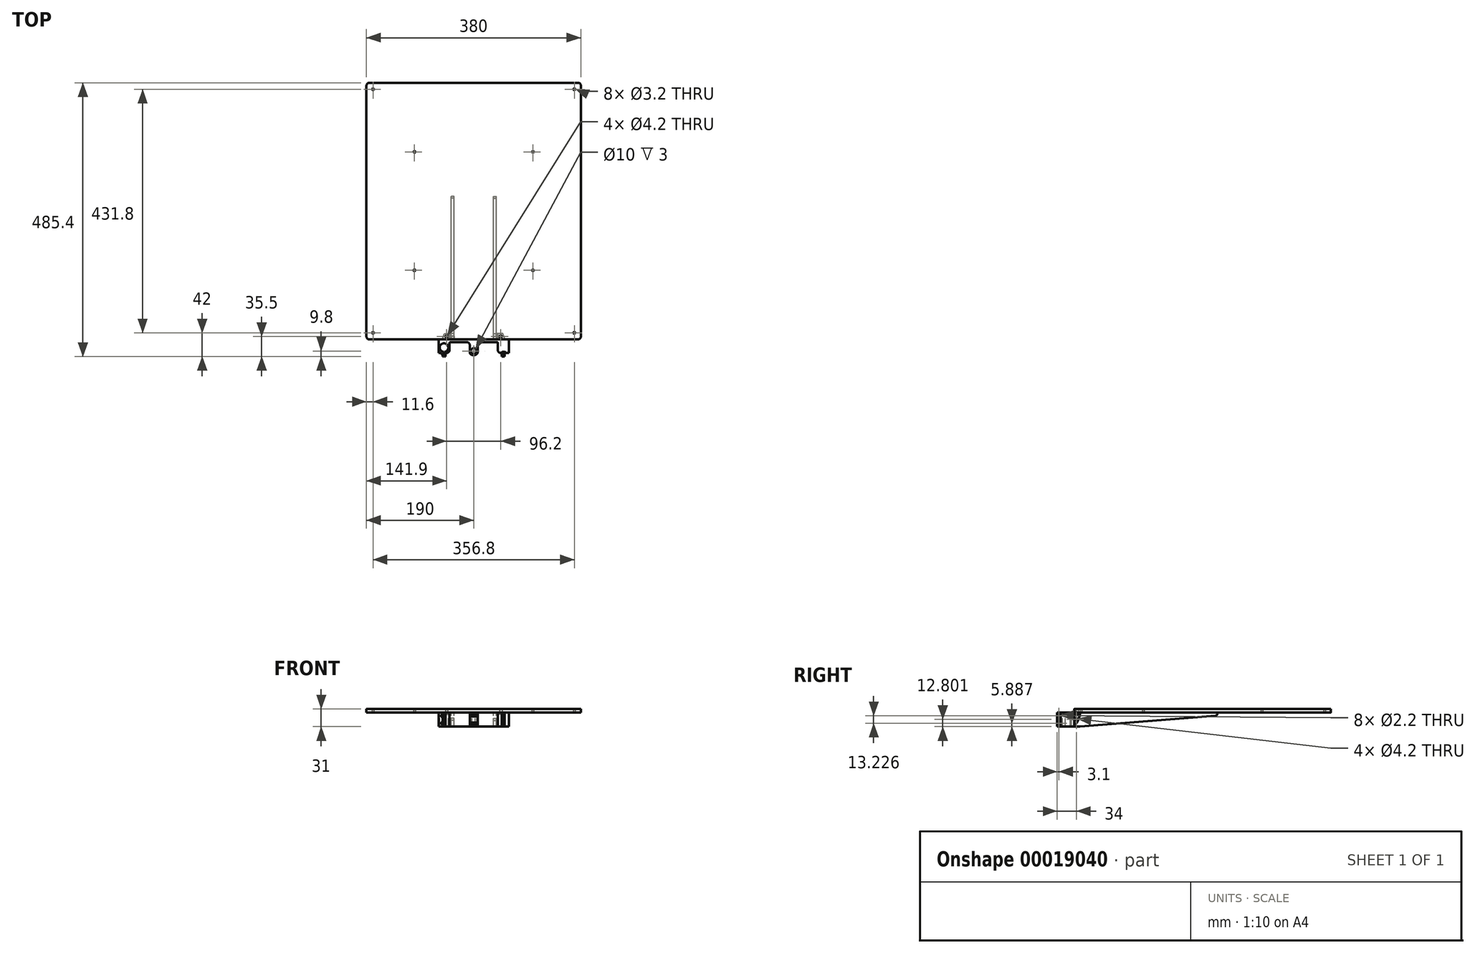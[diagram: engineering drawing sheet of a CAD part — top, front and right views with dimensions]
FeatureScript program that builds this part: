
annotation { "Feature Type Name" : "Feature", "Feature Type Description" : "" }
export const myFeature = defineFeature(function(context is Context, id is Id, definition is map)
    precondition{}
    {
        {
            var Q0;
            Q0=qCreatedBy(makeId("Top.planeOp"),FACE);
            var sketch = newSketch(context, id + "F0", { "sketchPlane" : qUnion([Q0])});
            skLineSegment(sketch, "E0.bottom", {"start": v(62.2, 0) * mm, "end": v(-62.2, 0) * mm});
            skLineSegment(sketch, "E0.top", {"start": v(62.2, 5) * mm, "end": v(-62.2, 5) * mm});
            skLineSegment(sketch, "E0.left", {"start": v(62.2, 0) * mm, "end": v(62.2, 5) * mm});
            skLineSegment(sketch, "E0.right", {"start": v(-62.2, 0) * mm, "end": v(-62.2, 5) * mm});
            skLineSegment(sketch, "E1", {"start": v(-55.38, 5) * mm, "end": v(-51.67, 15.2) * mm});
            skLineSegment(sketch, "E2", {"start": v(-51.67, 15.2) * mm, "end": v(-43, 15.2) * mm});
            skLineSegment(sketch, "E3", {"start": v(-43, 15.2) * mm, "end": v(-43, 5) * mm});
            skLineSegment(sketch, "E4", {"start": v(-48.1, 15.2) * mm, "end": v(-48.1, 5) * mm, "construction": true});
            skCircle(sketch, "E5", {"center": v(-48.1, 10.1) * mm, "radius": 2.1 * mm});
            skCircle(sketch, "E6", {"center": v(-52.6, -9.6) * mm, "radius": 7.6 * mm});
            skLineSegment(sketch, "E7", {"start": v(0, 10.4) * mm, "end": v(0, -22.6) * mm, "construction": true});
            skLineSegment(sketch, "E8.MirrorCS", {"start": v(55.38, 5) * mm, "end": v(51.67, 15.2) * mm});
            skLineSegment(sketch, "E9.MirrorCS", {"start": v(43, 15.2) * mm, "end": v(43, 5) * mm});
            skLineSegment(sketch, "E10.MirrorCS", {"start": v(51.67, 15.2) * mm, "end": v(43, 15.2) * mm});
            skCircle(sketch, "E11.MirrorC", {"center": v(48.1, 10.1) * mm, "radius": 2.1 * mm});
            skCircle(sketch, "E12.MirrorC", {"center": v(52.6, -9.6) * mm, "radius": 7.6 * mm});
            skCircle(sketch, "E13", {"center": v(0, -15.6) * mm, "radius": 5 * mm});
            skLineSegment(sketch, "E14", {"start": v(-62.2, 0) * mm, "end": v(-62.2, -19.2) * mm});
            skLineSegment(sketch, "E15", {"start": v(-62.2, -19.2) * mm, "end": v(-43, -19.2) * mm});
            skLineSegment(sketch, "E16", {"start": v(-43, -19.2) * mm, "end": v(-43, 5) * mm});
            skLineSegment(sketch, "E17.MirrorCS", {"start": v(62.2, -19.2) * mm, "end": v(43, -19.2) * mm});
            skLineSegment(sketch, "E18.MirrorCS", {"start": v(43, -19.2) * mm, "end": v(43, 5) * mm});
            skLineSegment(sketch, "E19.MirrorCS", {"start": v(62.2, 0) * mm, "end": v(62.2, -19.2) * mm});
            skCircle(sketch, "E20.cCircle", {"center": v(0, -15.6) * mm, "radius": 5 * mm, "construction": true});
            skLineSegment(sketch, "E20.0", {"start": v(-2.89, -20.6) * mm, "end": v(-5.77, -15.6) * mm});
            skLineSegment(sketch, "E20.1", {"start": v(-5.77, -15.6) * mm, "end": v(-2.89, -10.6) * mm});
            skLineSegment(sketch, "E20.2", {"start": v(-2.89, -10.6) * mm, "end": v(2.89, -10.6) * mm});
            skLineSegment(sketch, "E20.3", {"start": v(2.89, -10.6) * mm, "end": v(5.77, -15.6) * mm});
            skLineSegment(sketch, "E20.4", {"start": v(5.77, -15.6) * mm, "end": v(2.89, -20.6) * mm});
            skLineSegment(sketch, "E20.5", {"start": v(2.89, -20.6) * mm, "end": v(-2.89, -20.6) * mm});
            skPoint(sketch, "E20.0.midPoint", {"position": v(-4.33, -18.1) * mm});
            skLineSegment(sketch, "E21", {"start": v(-7, 0) * mm, "end": v(-7, -22.6) * mm});
            skLineSegment(sketch, "E22", {"start": v(-7, -22.6) * mm, "end": v(7, -22.6) * mm});
            skLineSegment(sketch, "E23", {"start": v(7, -22.6) * mm, "end": v(7, 0) * mm});
            skLineSegment(sketch, "E24", {"start": v(-52.6, -9.6) * mm, "end": v(52.6, -9.6) * mm, "construction": true});
            skLineSegment(sketch, "E25", {"start": v(-55.1, -16.78) * mm, "end": v(-55.1, -25.4) * mm});
            skLineSegment(sketch, "E26", {"start": v(-55.1, -25.4) * mm, "end": v(-53.1, -25.4) * mm});
            skLineSegment(sketch, "E27", {"start": v(-53.1, -25.4) * mm, "end": v(-53.1, -17.18) * mm});
            skLineSegment(sketch, "E28", {"start": v(-52.6, -34.95) * mm, "end": v(-52.6, -9.6) * mm, "construction": true});
            skLineSegment(sketch, "E29.MirrorCS", {"start": v(-50.1, -16.78) * mm, "end": v(-50.1, -25.4) * mm});
            skLineSegment(sketch, "E30.MirrorCS", {"start": v(-52.1, -25.4) * mm, "end": v(-52.1, -17.18) * mm});
            skLineSegment(sketch, "E31.MirrorCS", {"start": v(-50.1, -25.4) * mm, "end": v(-52.1, -25.4) * mm});
            skLineSegment(sketch, "E32.MirrorCS", {"start": v(55.1, -16.78) * mm, "end": v(55.1, -25.4) * mm});
            skLineSegment(sketch, "E33.MirrorCS", {"start": v(53.1, -25.4) * mm, "end": v(53.1, -17.18) * mm});
            skLineSegment(sketch, "E34.MirrorCS", {"start": v(52.1, -25.4) * mm, "end": v(52.1, -17.18) * mm});
            skLineSegment(sketch, "E35.MirrorCS", {"start": v(50.1, -16.78) * mm, "end": v(50.1, -25.4) * mm});
            skLineSegment(sketch, "E36.MirrorCS", {"start": v(50.1, -25.4) * mm, "end": v(52.1, -25.4) * mm});
            skLineSegment(sketch, "E37.MirrorCS", {"start": v(55.1, -25.4) * mm, "end": v(53.1, -25.4) * mm});
            skLineSegment(sketch, "E38", {"start": v(0, -10.6) * mm, "end": v(0, 0) * mm, "construction": true});
            skLineSegment(sketch, "E39.bottom", {"start": v(-185, 5) * mm, "end": v(185, 5) * mm});
            skLineSegment(sketch, "E39.top", {"start": v(-185, 460) * mm, "end": v(185, 460) * mm});
            skLineSegment(sketch, "E39.left", {"start": v(-190, 455) * mm, "end": v(-190, 10) * mm});
            skLineSegment(sketch, "E39.right", {"start": v(190, 455) * mm, "end": v(190, 10) * mm});
            skPoint(sketch, "E40.visualSharp", {"position": v(-190, 5) * mm});
            skArc(sketch, "E40.filletArc", {"start": v(-190, 10) * mm, "mid": v(-188.54, 6.46) * mm, "end": v(-185, 5) * mm});
            skPoint(sketch, "E41.visualSharp", {"position": v(190, 5) * mm});
            skArc(sketch, "E41.filletArc", {"start": v(185, 5) * mm, "mid": v(188.54, 6.46) * mm, "end": v(190, 10) * mm});
            skPoint(sketch, "E42.visualSharp", {"position": v(190, 460) * mm});
            skArc(sketch, "E42.filletArc", {"start": v(190, 455) * mm, "mid": v(188.54, 458.54) * mm, "end": v(185, 460) * mm});
            skPoint(sketch, "E43.visualSharp", {"position": v(-190, 460) * mm});
            skArc(sketch, "E43.filletArc", {"start": v(-185, 460) * mm, "mid": v(-188.54, 458.54) * mm, "end": v(-190, 455) * mm});
            skPoint(sketch, "E44.endSnap0", {"position": v(53.53, 10.1) * mm});
            skLineSegment(sketch, "E45", {"start": v(52.6, -2) * mm, "end": v(52.6, 10.4) * mm, "construction": true});
            skLineSegment(sketch, "E46", {"start": v(52.6, 10.4) * mm, "end": v(0, 10.4) * mm, "construction": true});
            skLineSegment(sketch, "E47", {"start": v(-190, 232.5) * mm, "end": v(190, 232.5) * mm, "construction": true});
            skLineSegment(sketch, "E48.rect.bottom", {"start": v(-105, 337.5) * mm, "end": v(105, 337.5) * mm, "construction": true});
            skLineSegment(sketch, "E48.rect.top", {"start": v(-105, 127.5) * mm, "end": v(105, 127.5) * mm, "construction": true});
            skLineSegment(sketch, "E48.rect.left", {"start": v(-105, 337.5) * mm, "end": v(-105, 127.5) * mm, "construction": true});
            skLineSegment(sketch, "E48.rect.right", {"start": v(105, 337.5) * mm, "end": v(105, 127.5) * mm, "construction": true});
            skPoint(sketch, "E48.rect.middle", {"position": v(0, 232.5) * mm});
            skCircle(sketch, "E49", {"center": v(-105, 337.5) * mm, "radius": 1.6 * mm});
            skCircle(sketch, "E50", {"center": v(105, 337.5) * mm, "radius": 1.6 * mm});
            skCircle(sketch, "E51", {"center": v(105, 127.5) * mm, "radius": 1.6 * mm});
            skCircle(sketch, "E52", {"center": v(-105, 127.5) * mm, "radius": 1.6 * mm});
            skCircle(sketch, "E53", {"center": v(-178.4, 448.4) * mm, "radius": 1.6 * mm});
            skCircle(sketch, "E54", {"center": v(178.4, 448.4) * mm, "radius": 1.6 * mm});
            skCircle(sketch, "E55", {"center": v(178.4, 16.6) * mm, "radius": 1.6 * mm});
            skCircle(sketch, "E56", {"center": v(-178.4, 16.6) * mm, "radius": 1.6 * mm});
            skSolve(sketch);
        }
        {
            var Q0;
            Q0=makeQuery(id+"F0.imprint","IMPRINT",FACE,{"disambiguationData":[TD([[makeQuery(id+"F0.imprint","IMPRINT",EDGE,{"derivedFrom":sQuery(id+"F0.wireOp",EDGE,"E0.bottom")}),-1.0]])]});
            var Q1;
            {var subQ5=sQuery(id+"F0.wireOp",EDGE,"E0.right");Q1=makeQuery(id+"F0.imprint","IMPRINT",FACE,{"disambiguationData":[TD([[makeQuery(id+"F0.imprint","IMPRINT",EDGE,{"derivedFrom":subQ5}),-1.0]])]});}
            var Q2;
            {var subQ5=sQuery(id+"F0.wireOp",EDGE,"E0.left");Q2=makeQuery(id+"F0.imprint","IMPRINT",FACE,{"disambiguationData":[TD([[makeQuery(id+"F0.imprint","IMPRINT",EDGE,{"derivedFrom":subQ5}),1.0]])]});}
            var Q3;
            {var subQ10=sQuery(id+"F0.wireOp",EDGE,"E14");Q3=makeQuery(id+"F0.imprint","IMPRINT",FACE,{"disambiguationData":[TD([[makeQuery(id+"F0.imprint","IMPRINT",EDGE,{"derivedFrom":subQ10}),1.0]])]});}
            var Q4;
            {var subQ3=sQuery(id+"F0.wireOp",EDGE,"E6");var subQ5=sQuery(id+"F0.wireOp",EDGE,"E29.MirrorCS");var subQ7=makeQuery(id+"F0.imprint","INTERSECT",VERTEX,{"derivedFrom":[subQ3,subQ5]});Q4=makeQuery(id+"F0.imprint","IMPRINT",FACE,{"disambiguationData":[TD([[makeQuery(id+"F0.imprint","IMPRINT",EDGE,{"disambiguationData":[TD([[subQ7,1.0]])],"derivedFrom":subQ3}),-1.0]])]});}
            var Q5;
            {var subQ3=sQuery(id+"F0.wireOp",EDGE,"E6");var subQ5=sQuery(id+"F0.wireOp",EDGE,"E25");var subQ7=makeQuery(id+"F0.imprint","INTERSECT",VERTEX,{"derivedFrom":[subQ3,subQ5]});Q5=makeQuery(id+"F0.imprint","IMPRINT",FACE,{"disambiguationData":[TD([[makeQuery(id+"F0.imprint","IMPRINT",EDGE,{"disambiguationData":[TD([[subQ7,-1.0]])],"derivedFrom":subQ3}),-1.0]])]});}
            var Q6;
            {var subQ3=sQuery(id+"F0.wireOp",EDGE,"E26");Q6=makeQuery(id+"F0.imprint","IMPRINT",FACE,{"disambiguationData":[TD([[makeQuery(id+"F0.imprint","IMPRINT",EDGE,{"derivedFrom":subQ3}),1.0]])]});}
            var Q7;
            {var subQ0=sQuery(id+"F0.wireOp",EDGE,"E31.MirrorCS");Q7=makeQuery(id+"F0.imprint","IMPRINT",FACE,{"disambiguationData":[TD([[makeQuery(id+"F0.imprint","IMPRINT",EDGE,{"derivedFrom":subQ0}),-1.0]])]});}
            var Q8;
            {var subQ12=sQuery(id+"F0.wireOp",EDGE,"E19.MirrorCS");Q8=makeQuery(id+"F0.imprint","IMPRINT",FACE,{"disambiguationData":[TD([[makeQuery(id+"F0.imprint","IMPRINT",EDGE,{"derivedFrom":subQ12}),-1.0]])]});}
            var Q9;
            {var subQ3=sQuery(id+"F0.wireOp",EDGE,"E12.MirrorC");var subQ5=sQuery(id+"F0.wireOp",EDGE,"E32.MirrorCS");var subQ7=makeQuery(id+"F0.imprint","INTERSECT",VERTEX,{"derivedFrom":[subQ3,subQ5]});Q9=makeQuery(id+"F0.imprint","IMPRINT",FACE,{"disambiguationData":[TD([[makeQuery(id+"F0.imprint","IMPRINT",EDGE,{"disambiguationData":[TD([[subQ7,-1.0]])],"derivedFrom":subQ3}),1.0]])]});}
            var Q10;
            {var subQ3=sQuery(id+"F0.wireOp",EDGE,"E12.MirrorC");var subQ5=sQuery(id+"F0.wireOp",EDGE,"E34.MirrorCS");var subQ7=makeQuery(id+"F0.imprint","INTERSECT",VERTEX,{"derivedFrom":[subQ3,subQ5]});Q10=makeQuery(id+"F0.imprint","IMPRINT",FACE,{"disambiguationData":[TD([[makeQuery(id+"F0.imprint","IMPRINT",EDGE,{"disambiguationData":[TD([[subQ7,-1.0]])],"derivedFrom":subQ3}),1.0]])]});}
            var Q11;
            {var subQ0=sQuery(id+"F0.wireOp",EDGE,"E36.MirrorCS");Q11=makeQuery(id+"F0.imprint","IMPRINT",FACE,{"disambiguationData":[TD([[makeQuery(id+"F0.imprint","IMPRINT",EDGE,{"derivedFrom":subQ0}),1.0]])]});}
            var Q12;
            {var subQ3=sQuery(id+"F0.wireOp",EDGE,"E37.MirrorCS");Q12=makeQuery(id+"F0.imprint","IMPRINT",FACE,{"disambiguationData":[TD([[makeQuery(id+"F0.imprint","IMPRINT",EDGE,{"derivedFrom":subQ3}),-1.0]])]});}
            var Q13;
            {var subQ10=sQuery(id+"F0.wireOp",EDGE,"E21");Q13=makeQuery(id+"F0.imprint","IMPRINT",FACE,{"disambiguationData":[TD([[makeQuery(id+"F0.imprint","IMPRINT",EDGE,{"derivedFrom":subQ10}),1.0]])]});}
            var Q14;
            {var subQ0=sQuery(id+"F0.wireOp",EDGE,"E20.2");var subQ1=sQuery(id+"F0.wireOp",EDGE,"E13");var subQ2=makeQuery(id+"F0.imprint","INTERSECT",VERTEX,{"derivedFrom":[subQ1,subQ0]});Q14=makeQuery(id+"F0.imprint","IMPRINT",FACE,{"disambiguationData":[TD([[makeQuery(id+"F0.imprint","IMPRINT",EDGE,{"disambiguationData":[TD([[subQ2,-1.0]])],"derivedFrom":subQ1}),-1.0]])]});}
            var Q15;
            {var subQ1=sQuery(id+"F0.wireOp",EDGE,"E13");var subQ3=sQuery(id+"F0.wireOp",EDGE,"E20.2");var subQ5=makeQuery(id+"F0.imprint","INTERSECT",VERTEX,{"derivedFrom":[subQ1,subQ3]});Q15=makeQuery(id+"F0.imprint","IMPRINT",FACE,{"disambiguationData":[TD([[makeQuery(id+"F0.imprint","IMPRINT",EDGE,{"disambiguationData":[TD([[subQ5,1.0]])],"derivedFrom":subQ1}),-1.0]])]});}
            var Q16;
            {var subQ0=sQuery(id+"F0.wireOp",EDGE,"E20.1");var subQ1=sQuery(id+"F0.wireOp",EDGE,"E13");var subQ2=makeQuery(id+"F0.imprint","INTERSECT",VERTEX,{"derivedFrom":[subQ1,subQ0]});Q16=makeQuery(id+"F0.imprint","IMPRINT",FACE,{"disambiguationData":[TD([[makeQuery(id+"F0.imprint","IMPRINT",EDGE,{"disambiguationData":[TD([[subQ2,-1.0]])],"derivedFrom":subQ1}),-1.0]])]});}
            var Q17;
            {var subQ1=sQuery(id+"F0.wireOp",EDGE,"E13");var subQ3=sQuery(id+"F0.wireOp",EDGE,"E20.3");var subQ5=makeQuery(id+"F0.imprint","INTERSECT",VERTEX,{"derivedFrom":[subQ1,subQ3]});Q17=makeQuery(id+"F0.imprint","IMPRINT",FACE,{"disambiguationData":[TD([[makeQuery(id+"F0.imprint","IMPRINT",EDGE,{"disambiguationData":[TD([[subQ5,1.0]])],"derivedFrom":subQ1}),-1.0]])]});}
            var Q18;
            {var subQ1=sQuery(id+"F0.wireOp",EDGE,"E13");var subQ3=sQuery(id+"F0.wireOp",EDGE,"E20.0");var subQ5=makeQuery(id+"F0.imprint","INTERSECT",VERTEX,{"derivedFrom":[subQ1,subQ3]});Q18=makeQuery(id+"F0.imprint","IMPRINT",FACE,{"disambiguationData":[TD([[makeQuery(id+"F0.imprint","IMPRINT",EDGE,{"disambiguationData":[TD([[subQ5,-1.0]])],"derivedFrom":subQ1}),-1.0]])]});}
            var Q19;
            {var subQ0=sQuery(id+"F0.wireOp",EDGE,"E20.5");var subQ1=sQuery(id+"F0.wireOp",EDGE,"E13");var subQ2=makeQuery(id+"F0.imprint","INTERSECT",VERTEX,{"derivedFrom":[subQ1,subQ0]});Q19=makeQuery(id+"F0.imprint","IMPRINT",FACE,{"disambiguationData":[TD([[makeQuery(id+"F0.imprint","IMPRINT",EDGE,{"disambiguationData":[TD([[subQ2,-1.0]])],"derivedFrom":subQ1}),-1.0]])]});}
            extrude(context, id + "F1", {"entities" : qUnion([Q0, Q1, Q2, Q3, Q4, Q5, Q6, Q7, Q8, Q9, Q10, Q11, Q12, Q13, Q14, Q15, Q16, Q17, Q18, Q19]), "oppositeDirection" : true, "depth" : 25 * mm});
        }
        {
            var Q0;
            {var subQ1=sQuery(id+"F0.wireOp",EDGE,"E1");Q0=makeQuery(id+"F0.imprint","IMPRINT",FACE,{"disambiguationData":[TD([[makeQuery(id+"F0.imprint","IMPRINT",EDGE,{"derivedFrom":subQ1}),-1.0]])]});}
            var Q1;
            {var subQ1=sQuery(id+"F0.wireOp",EDGE,"E8.MirrorCS");Q1=makeQuery(id+"F0.imprint","IMPRINT",FACE,{"disambiguationData":[TD([[makeQuery(id+"F0.imprint","IMPRINT",EDGE,{"derivedFrom":subQ1}),1.0]])]});}
            extrude(context, id + "F2", {"entities" : qUnion([Q0, Q1]), "operationType" : NewBodyOperationType.ADD, "oppositeDirection" : true, "depth" : 3 * mm});
        }
        {
            var Q0;
            {var subQ0=sQuery(id+"F0.wireOp",EDGE,"E20.2");var subQ1=sQuery(id+"F0.wireOp",EDGE,"E13");var subQ2=makeQuery(id+"F0.imprint","INTERSECT",VERTEX,{"derivedFrom":[subQ1,subQ0]});Q0=makeQuery(id+"F0.imprint","IMPRINT",FACE,{"disambiguationData":[TD([[makeQuery(id+"F0.imprint","IMPRINT",EDGE,{"disambiguationData":[TD([[subQ2,-1.0]])],"derivedFrom":subQ1}),-1.0]])]});}
            var Q1;
            {var subQ1=sQuery(id+"F0.wireOp",EDGE,"E13");var subQ3=sQuery(id+"F0.wireOp",EDGE,"E20.2");var subQ5=makeQuery(id+"F0.imprint","INTERSECT",VERTEX,{"derivedFrom":[subQ1,subQ3]});Q1=makeQuery(id+"F0.imprint","IMPRINT",FACE,{"disambiguationData":[TD([[makeQuery(id+"F0.imprint","IMPRINT",EDGE,{"disambiguationData":[TD([[subQ5,1.0]])],"derivedFrom":subQ1}),-1.0]])]});}
            var Q2;
            {var subQ1=sQuery(id+"F0.wireOp",EDGE,"E13");var subQ3=sQuery(id+"F0.wireOp",EDGE,"E20.3");var subQ5=makeQuery(id+"F0.imprint","INTERSECT",VERTEX,{"derivedFrom":[subQ1,subQ3]});Q2=makeQuery(id+"F0.imprint","IMPRINT",FACE,{"disambiguationData":[TD([[makeQuery(id+"F0.imprint","IMPRINT",EDGE,{"disambiguationData":[TD([[subQ5,1.0]])],"derivedFrom":subQ1}),-1.0]])]});}
            var Q3;
            {var subQ0=sQuery(id+"F0.wireOp",EDGE,"E20.5");var subQ1=sQuery(id+"F0.wireOp",EDGE,"E13");var subQ2=makeQuery(id+"F0.imprint","INTERSECT",VERTEX,{"derivedFrom":[subQ1,subQ0]});Q3=makeQuery(id+"F0.imprint","IMPRINT",FACE,{"disambiguationData":[TD([[makeQuery(id+"F0.imprint","IMPRINT",EDGE,{"disambiguationData":[TD([[subQ2,-1.0]])],"derivedFrom":subQ1}),-1.0]])]});}
            var Q4;
            {var subQ0=sQuery(id+"F0.wireOp",EDGE,"E20.1");var subQ1=sQuery(id+"F0.wireOp",EDGE,"E13");var subQ2=makeQuery(id+"F0.imprint","INTERSECT",VERTEX,{"derivedFrom":[subQ1,subQ0]});Q4=makeQuery(id+"F0.imprint","IMPRINT",FACE,{"disambiguationData":[TD([[makeQuery(id+"F0.imprint","IMPRINT",EDGE,{"disambiguationData":[TD([[subQ2,-1.0]])],"derivedFrom":subQ1}),-1.0]])]});}
            var Q5;
            {var subQ1=sQuery(id+"F0.wireOp",EDGE,"E13");var subQ3=sQuery(id+"F0.wireOp",EDGE,"E20.0");var subQ5=makeQuery(id+"F0.imprint","INTERSECT",VERTEX,{"derivedFrom":[subQ1,subQ3]});Q5=makeQuery(id+"F0.imprint","IMPRINT",FACE,{"disambiguationData":[TD([[makeQuery(id+"F0.imprint","IMPRINT",EDGE,{"disambiguationData":[TD([[subQ5,-1.0]])],"derivedFrom":subQ1}),-1.0]])]});}
            var Q6;
            Q6=makeQuery(id+"F1.opExtrude","CAP_FACE",FACE,{"disambiguationData":[OSD([sQuery(id+"F0.wireOp",EDGE,"E0.bottom"),sQuery(id+"F0.wireOp",EDGE,"E0.left"),sQuery(id+"F0.wireOp",EDGE,"E0.right"),sQuery(id+"F0.wireOp",EDGE,"E6"),sQuery(id+"F0.wireOp",EDGE,"E12.MirrorC"),sQuery(id+"F0.wireOp",EDGE,"E13"),sQuery(id+"F0.wireOp",EDGE,"E14"),sQuery(id+"F0.wireOp",EDGE,"E15"),sQuery(id+"F0.wireOp",EDGE,"E16"),sQuery(id+"F0.wireOp",EDGE,"E17.MirrorCS"),sQuery(id+"F0.wireOp",EDGE,"E18.MirrorCS"),sQuery(id+"F0.wireOp",EDGE,"E19.MirrorCS"),sQuery(id+"F0.wireOp",EDGE,"E21"),sQuery(id+"F0.wireOp",EDGE,"E22"),sQuery(id+"F0.wireOp",EDGE,"E23"),sQuery(id+"F0.wireOp",EDGE,"E25"),sQuery(id+"F0.wireOp",EDGE,"E26"),sQuery(id+"F0.wireOp",EDGE,"E27"),sQuery(id+"F0.wireOp",EDGE,"E29.MirrorCS"),sQuery(id+"F0.wireOp",EDGE,"E30.MirrorCS"),sQuery(id+"F0.wireOp",EDGE,"E31.MirrorCS"),sQuery(id+"F0.wireOp",EDGE,"E32.MirrorCS"),sQuery(id+"F0.wireOp",EDGE,"E33.MirrorCS"),sQuery(id+"F0.wireOp",EDGE,"E34.MirrorCS"),sQuery(id+"F0.wireOp",EDGE,"E35.MirrorCS"),sQuery(id+"F0.wireOp",EDGE,"E36.MirrorCS"),sQuery(id+"F0.wireOp",EDGE,"E37.MirrorCS"),sQuery(id+"F0.wireOp",EDGE,"E39.bottom")])],"isStart":false});
            extrude(context, id + "F3", {"entities" : qUnion([Q0, Q1, Q2, Q3, Q4, Q5]), "operationType" : NewBodyOperationType.REMOVE, "endBound" : BoundingType.UP_TO_SURFACE, "oppositeDirection" : true, "endBoundEntityFace" : qUnion([Q6]), "depth" : 25 * mm, "hasSecondDirection" : true, "secondDirectionOppositeDirection" : true, "secondDirectionDepth" : 3 * mm});
        }
        {
            var Q0;
            Q0=makeQuery(id+"F2.opExtrude","SWEPT_FACE",FACE,{"disambiguationData":[OSD([sQuery(id+"F0.wireOp",EDGE,"E3")])]});
            var sketch = newSketch(context, id + "F4", { "sketchPlane" : qUnion([Q0])});
            skLineSegment(sketch, "E57.0", {"start": v(5, -25) * mm, "end": v(5, 0) * mm});
            skLineSegment(sketch, "E57.1", {"start": v(15.2, -3) * mm, "end": v(5, -3) * mm});
            skArc(sketch, "E58", {"start": v(5, -25) * mm, "mid": v(11.45, -14.63) * mm, "end": v(15.2, -3) * mm});
            skCircle(sketch, "E59", {"center": v(8.6, -12.2) * mm, "radius": 2.1 * mm});
            skSolve(sketch);
        }
        {
            var Q0;
            {var subQ1=sQuery(id+"F4.wireOp",EDGE,"E57.1");Q0=makeQuery(id+"F4.imprint","IMPRINT",FACE,{"disambiguationData":[TD([[makeQuery(id+"F4.imprint","IMPRINT",EDGE,{"derivedFrom":subQ1}),1.0]])]});}
            var Q1;
            {var subQ2=sQuery(id+"F4.wireOp",EDGE,"E57.1");Q1=makeQuery(id+"F4.imprint","IMPRINT",FACE,{"disambiguationData":[TD([[makeQuery(id+"F4.imprint","IMPRINT",EDGE,{"derivedFrom":subQ2}),-1.0]])]});}
            var Q2;
            {var subQ0=sQuery(id+"F0.wireOp",EDGE,"E3");var subQ1=makeQuery(id+"F2.opExtrude","CAP_EDGE",EDGE,{"disambiguationData":[OSD([subQ0])],"isStart":true});Q2=makeQuery(id+"F4.imprint","IMPRINT",FACE,{"disambiguationData":[TD([[makeQuery(id+"F4.imprint","IMPRINT",EDGE,{"derivedFrom":subQ1}),1.0]])]});}
            var Q3;
            {var subQ3=sQuery(id+"F4.wireOp",EDGE,"E58");Q3=makeQuery(id+"F4.imprint","IMPRINT",FACE,{"disambiguationData":[TD([[makeQuery(id+"F4.imprint","IMPRINT",EDGE,{"derivedFrom":subQ3}),1.0]])]});}
            extrude(context, id + "F5", {"entities" : qUnion([Q0, Q1, Q2, Q3]), "depth" : 3 * mm});
        }
        {
            var Q0;
            Q0=makeQuery(id+"F5.opExtrude","SWEPT_BODY",BODY,{"disambiguationData":[OSD([sQuery(id+"F0.wireOp",EDGE,"E2"),sQuery(id+"F0.wireOp",EDGE,"E3"),sQuery(id+"F4.wireOp",EDGE,"E57.0"),sQuery(id+"F4.wireOp",EDGE,"E58"),sQuery(id+"F4.wireOp",EDGE,"E59")])]});
            var Q1;
            Q1=qCreatedBy(makeId("Right.planeOp"),FACE);
            mirror(context, id + "F6", {"operationType" : NewBodyOperationType.ADD, "entities" : qUnion([Q0]), "mirrorPlane" : qUnion([Q1])});
        }
        {
            var Q0;
            Q0=makeQuery(id+"F1.opExtrude","SWEPT_FACE",FACE,{"disambiguationData":[OSD([sQuery(id+"F0.wireOp",EDGE,"E25")])]});
            var sketch = newSketch(context, id + "F7", { "sketchPlane" : qUnion([Q0])});
            skCircle(sketch, "E60.cCircle", {"center": v(22.3, -5.89) * mm, "radius": 2.5 * mm, "construction": true});
            skLineSegment(sketch, "E60.0", {"start": v(19.8, -4.44) * mm, "end": v(22.3, -3) * mm});
            skLineSegment(sketch, "E60.1", {"start": v(22.3, -3) * mm, "end": v(24.8, -4.44) * mm});
            skLineSegment(sketch, "E60.2", {"start": v(24.8, -4.44) * mm, "end": v(24.8, -7.33) * mm});
            skLineSegment(sketch, "E60.3", {"start": v(24.8, -7.33) * mm, "end": v(22.3, -8.77) * mm});
            skLineSegment(sketch, "E60.4", {"start": v(22.3, -8.77) * mm, "end": v(19.8, -7.33) * mm});
            skLineSegment(sketch, "E60.5", {"start": v(19.8, -7.33) * mm, "end": v(19.8, -4.44) * mm});
            skPoint(sketch, "E60.0.midPoint", {"position": v(21.05, -3.72) * mm});
            skLineSegment(sketch, "E61", {"start": v(19.2, -5.89) * mm, "end": v(25.4, -5.89) * mm, "construction": true});
            skCircle(sketch, "E62.cCircle", {"center": v(22.3, -19.11) * mm, "radius": 2.5 * mm, "construction": true});
            skLineSegment(sketch, "E62.0", {"start": v(22.3, -22) * mm, "end": v(19.8, -20.56) * mm});
            skLineSegment(sketch, "E62.1", {"start": v(19.8, -20.56) * mm, "end": v(19.8, -17.67) * mm});
            skLineSegment(sketch, "E62.2", {"start": v(19.8, -17.67) * mm, "end": v(22.3, -16.23) * mm});
            skLineSegment(sketch, "E62.3", {"start": v(22.3, -16.23) * mm, "end": v(24.8, -17.67) * mm});
            skLineSegment(sketch, "E62.4", {"start": v(24.8, -17.67) * mm, "end": v(24.8, -20.56) * mm});
            skLineSegment(sketch, "E62.5", {"start": v(24.8, -20.56) * mm, "end": v(22.3, -22) * mm});
            skPoint(sketch, "E62.0.midPoint", {"position": v(21.05, -21.28) * mm});
            skLineSegment(sketch, "E63", {"start": v(19.2, -19.11) * mm, "end": v(25.4, -19.11) * mm, "construction": true});
            skCircle(sketch, "E64", {"center": v(22.3, -5.89) * mm, "radius": 1.1 * mm});
            skCircle(sketch, "E65", {"center": v(22.3, -19.11) * mm, "radius": 1.1 * mm});
            skSolve(sketch);
        }
        {
            var Q0;
            Q0=makeQuery(id+"F1.opExtrude","SWEPT_FACE",FACE,{"disambiguationData":[OSD([sQuery(id+"F0.wireOp",EDGE,"E32.MirrorCS")])]});
            var sketch = newSketch(context, id + "F8", { "sketchPlane" : qUnion([Q0])});
            skLineSegment(sketch, "E66.0", {"start": v(-22.3, -8.77) * mm, "end": v(-19.8, -7.33) * mm});
            skLineSegment(sketch, "E66.1", {"start": v(-24.8, -7.33) * mm, "end": v(-22.3, -8.77) * mm});
            skLineSegment(sketch, "E66.2", {"start": v(-24.8, -4.44) * mm, "end": v(-24.8, -7.33) * mm});
            skLineSegment(sketch, "E66.3", {"start": v(-22.3, -3) * mm, "end": v(-24.8, -4.44) * mm});
            skLineSegment(sketch, "E66.4", {"start": v(-19.8, -4.44) * mm, "end": v(-22.3, -3) * mm});
            skLineSegment(sketch, "E66.5", {"start": v(-19.8, -7.33) * mm, "end": v(-19.8, -4.44) * mm});
            skLineSegment(sketch, "E66.6", {"start": v(-19.8, -17.67) * mm, "end": v(-22.3, -16.23) * mm});
            skLineSegment(sketch, "E66.7", {"start": v(-22.3, -16.23) * mm, "end": v(-24.8, -17.67) * mm});
            skLineSegment(sketch, "E66.8", {"start": v(-24.8, -17.67) * mm, "end": v(-24.8, -20.56) * mm});
            skLineSegment(sketch, "E66.9", {"start": v(-24.8, -20.56) * mm, "end": v(-22.3, -22) * mm});
            skLineSegment(sketch, "E66.10", {"start": v(-22.3, -22) * mm, "end": v(-19.8, -20.56) * mm});
            skLineSegment(sketch, "E66.11", {"start": v(-19.8, -20.56) * mm, "end": v(-19.8, -17.67) * mm});
            skPoint(sketch, "E67.0", {"position": v(-22.3, -5.89) * mm});
            skPoint(sketch, "E67.1", {"position": v(-22.3, -19.11) * mm});
            skSolve(sketch);
        }
        {
            var Q0;
            Q0=makeQuery(id+"F7.imprint","IMPRINT",FACE,{"disambiguationData":[TD([[makeQuery(id+"F7.imprint","IMPRINT",EDGE,{"derivedFrom":sQuery(id+"F7.wireOp",EDGE,"E60.0")}),-1.0]])]});
            var Q1;
            Q1=makeQuery(id+"F7.imprint","IMPRINT",FACE,{"disambiguationData":[TD([[makeQuery(id+"F7.imprint","IMPRINT",EDGE,{"derivedFrom":sQuery(id+"F7.wireOp",EDGE,"E62.0")}),-1.0]])]});
            extrude(context, id + "F9", {"entities" : qUnion([Q0, Q1]), "operationType" : NewBodyOperationType.REMOVE, "oppositeDirection" : true, "depth" : 1 * mm});
        }
        {
            var Q0;
            Q0=makeQuery(id+"F9.boolean.opBoolean","SPLIT",FACE,{"disambiguationData":[TD([makeQuery(id+"F9.opExtrude","SWEPT_FACE",FACE,{"disambiguationData":[OSD([sQuery(id+"F7.wireOp",EDGE,"E64")])]})])],"derivedFrom":makeQuery(id+"F1.opExtrude","SWEPT_FACE",FACE,{"disambiguationData":[OSD([sQuery(id+"F0.wireOp",EDGE,"E25")])]})});
            var Q1;
            Q1=makeQuery(id+"F9.boolean.opBoolean","SPLIT",FACE,{"disambiguationData":[TD([makeQuery(id+"F9.opExtrude","SWEPT_FACE",FACE,{"disambiguationData":[OSD([sQuery(id+"F7.wireOp",EDGE,"E65")])]})])],"derivedFrom":makeQuery(id+"F1.opExtrude","SWEPT_FACE",FACE,{"disambiguationData":[OSD([sQuery(id+"F0.wireOp",EDGE,"E25")])]})});
            extrude(context, id + "F10", {"entities" : qUnion([Q0, Q1]), "operationType" : NewBodyOperationType.REMOVE, "endBound" : BoundingType.THROUGH_ALL, "oppositeDirection" : true, "depth" : 25 * mm});
        }
        {
            var Q0;
            Q0=makeQuery(id+"F8.imprint","IMPRINT",FACE,{"disambiguationData":[TD([[makeQuery(id+"F8.imprint","IMPRINT",EDGE,{"derivedFrom":sQuery(id+"F8.wireOp",EDGE,"E66.0")}),1.0]])]});
            var Q1;
            Q1=makeQuery(id+"F8.imprint","IMPRINT",FACE,{"disambiguationData":[TD([[makeQuery(id+"F8.imprint","IMPRINT",EDGE,{"derivedFrom":sQuery(id+"F8.wireOp",EDGE,"E66.6")}),1.0]])]});
            extrude(context, id + "F11", {"entities" : qUnion([Q0, Q1]), "operationType" : NewBodyOperationType.REMOVE, "oppositeDirection" : true, "depth" : 1 * mm});
        }
        {
            var Q0;
            {var subQ0=sQuery(id+"F0.wireOp",EDGE,"E21");var subQ1=sQuery(id+"F0.wireOp",EDGE,"E22");var subQ2=sQuery(id+"F0.wireOp",EDGE,"E39.bottom");var subQ3=sQuery(id+"F0.wireOp",EDGE,"E3");var subQ4=makeQuery(id+"F5.opExtrude","SWEPT_FACE",FACE,{"disambiguationData":[OSD([subQ3])]});Q0=makeQuery(id+"F10.boolean.opBoolean","SPLIT",EDGE,{"disambiguationData":[TD([makeQuery(id+"F1.opExtrude","CAP_FACE",FACE,{"disambiguationData":[OSD([sQuery(id+"F0.wireOp",EDGE,"E0.bottom"),sQuery(id+"F0.wireOp",EDGE,"E0.left"),sQuery(id+"F0.wireOp",EDGE,"E0.right"),sQuery(id+"F0.wireOp",EDGE,"E6"),sQuery(id+"F0.wireOp",EDGE,"E12.MirrorC"),sQuery(id+"F0.wireOp",EDGE,"E13"),sQuery(id+"F0.wireOp",EDGE,"E14"),sQuery(id+"F0.wireOp",EDGE,"E15"),sQuery(id+"F0.wireOp",EDGE,"E16"),sQuery(id+"F0.wireOp",EDGE,"E17.MirrorCS"),sQuery(id+"F0.wireOp",EDGE,"E18.MirrorCS"),sQuery(id+"F0.wireOp",EDGE,"E19.MirrorCS"),subQ0,subQ1,sQuery(id+"F0.wireOp",EDGE,"E23"),sQuery(id+"F0.wireOp",EDGE,"E25"),sQuery(id+"F0.wireOp",EDGE,"E26"),sQuery(id+"F0.wireOp",EDGE,"E27"),sQuery(id+"F0.wireOp",EDGE,"E29.MirrorCS"),sQuery(id+"F0.wireOp",EDGE,"E30.MirrorCS"),sQuery(id+"F0.wireOp",EDGE,"E31.MirrorCS"),sQuery(id+"F0.wireOp",EDGE,"E32.MirrorCS"),sQuery(id+"F0.wireOp",EDGE,"E33.MirrorCS"),sQuery(id+"F0.wireOp",EDGE,"E34.MirrorCS"),sQuery(id+"F0.wireOp",EDGE,"E35.MirrorCS"),sQuery(id+"F0.wireOp",EDGE,"E36.MirrorCS"),sQuery(id+"F0.wireOp",EDGE,"E37.MirrorCS"),subQ2])],"isStart":true}),makeQuery(id+"F1.opExtrude","SWEPT_FACE",FACE,{"disambiguationData":[OSD([subQ0])]}),makeQuery(id+"F1.opExtrude","SWEPT_FACE",FACE,{"disambiguationData":[OSD([subQ1])]}),makeQuery(id+"F2.opExtrude","CAP_FACE",FACE,{"disambiguationData":[OSD([sQuery(id+"F0.wireOp",EDGE,"E1"),sQuery(id+"F0.wireOp",EDGE,"E2"),subQ3,sQuery(id+"F0.wireOp",EDGE,"E5"),subQ2])],"isStart":true}),makeQuery(id+"F2.opExtrude","CAP_FACE",FACE,{"disambiguationData":[OSD([sQuery(id+"F0.wireOp",EDGE,"E8.MirrorCS"),sQuery(id+"F0.wireOp",EDGE,"E9.MirrorCS"),sQuery(id+"F0.wireOp",EDGE,"E10.MirrorCS"),sQuery(id+"F0.wireOp",EDGE,"E11.MirrorC"),subQ2])],"isStart":true}),subQ4,makeQuery(id+"F6.opPattern","COPY",FACE,{"derivedFrom":subQ4,"instanceName":"1"}),makeQuery(id+"F10.opExtrude","SWEPT_FACE",FACE,{"disambiguationData":[OSD([sQuery(id+"F7.wireOp",EDGE,"E64")])]})])],"derivedFrom":makeQuery(id+"F1.opExtrude","SWEPT_EDGE",EDGE,{"disambiguationData":[OSD([subQ0,subQ1])]})});}
            var Q1;
            {var subQ0=sQuery(id+"F0.wireOp",EDGE,"E21");var subQ1=sQuery(id+"F0.wireOp",EDGE,"E22");Q1=makeQuery(id+"F10.boolean.opBoolean","SPLIT",EDGE,{"disambiguationData":[TD([makeQuery(id+"F1.opExtrude","CAP_FACE",FACE,{"disambiguationData":[OSD([sQuery(id+"F0.wireOp",EDGE,"E0.bottom"),sQuery(id+"F0.wireOp",EDGE,"E0.left"),sQuery(id+"F0.wireOp",EDGE,"E0.right"),sQuery(id+"F0.wireOp",EDGE,"E6"),sQuery(id+"F0.wireOp",EDGE,"E12.MirrorC"),sQuery(id+"F0.wireOp",EDGE,"E13"),sQuery(id+"F0.wireOp",EDGE,"E14"),sQuery(id+"F0.wireOp",EDGE,"E15"),sQuery(id+"F0.wireOp",EDGE,"E16"),sQuery(id+"F0.wireOp",EDGE,"E17.MirrorCS"),sQuery(id+"F0.wireOp",EDGE,"E18.MirrorCS"),sQuery(id+"F0.wireOp",EDGE,"E19.MirrorCS"),subQ0,subQ1,sQuery(id+"F0.wireOp",EDGE,"E23"),sQuery(id+"F0.wireOp",EDGE,"E25"),sQuery(id+"F0.wireOp",EDGE,"E26"),sQuery(id+"F0.wireOp",EDGE,"E27"),sQuery(id+"F0.wireOp",EDGE,"E29.MirrorCS"),sQuery(id+"F0.wireOp",EDGE,"E30.MirrorCS"),sQuery(id+"F0.wireOp",EDGE,"E31.MirrorCS"),sQuery(id+"F0.wireOp",EDGE,"E32.MirrorCS"),sQuery(id+"F0.wireOp",EDGE,"E33.MirrorCS"),sQuery(id+"F0.wireOp",EDGE,"E34.MirrorCS"),sQuery(id+"F0.wireOp",EDGE,"E35.MirrorCS"),sQuery(id+"F0.wireOp",EDGE,"E36.MirrorCS"),sQuery(id+"F0.wireOp",EDGE,"E37.MirrorCS"),sQuery(id+"F0.wireOp",EDGE,"E39.bottom")])],"isStart":false}),makeQuery(id+"F1.opExtrude","SWEPT_FACE",FACE,{"disambiguationData":[OSD([subQ0])]}),makeQuery(id+"F1.opExtrude","SWEPT_FACE",FACE,{"disambiguationData":[OSD([subQ1])]}),makeQuery(id+"F10.opExtrude","SWEPT_FACE",FACE,{"disambiguationData":[OSD([sQuery(id+"F7.wireOp",EDGE,"E65")])]})])],"derivedFrom":makeQuery(id+"F1.opExtrude","SWEPT_EDGE",EDGE,{"disambiguationData":[OSD([subQ0,subQ1])]})});}
            var Q2;
            Q2=makeQuery(id+"F1.opExtrude","SWEPT_EDGE",EDGE,{"disambiguationData":[OSD([sQuery(id+"F0.wireOp",EDGE,"E15"),sQuery(id+"F0.wireOp",EDGE,"E25")])]});
            var Q3;
            Q3=makeQuery(id+"F1.opExtrude","SWEPT_EDGE",EDGE,{"disambiguationData":[OSD([sQuery(id+"F0.wireOp",EDGE,"E17.MirrorCS"),sQuery(id+"F0.wireOp",EDGE,"E32.MirrorCS")])]});
            var Q4;
            Q4=makeQuery(id+"F1.opExtrude","SWEPT_EDGE",EDGE,{"disambiguationData":[OSD([sQuery(id+"F0.wireOp",EDGE,"E15"),sQuery(id+"F0.wireOp",EDGE,"E16")])]});
            var Q5;
            {var subQ0=sQuery(id+"F0.wireOp",EDGE,"E22");var subQ1=sQuery(id+"F0.wireOp",EDGE,"E23");var subQ2=sQuery(id+"F0.wireOp",EDGE,"E3");var subQ3=makeQuery(id+"F5.opExtrude","SWEPT_FACE",FACE,{"disambiguationData":[OSD([subQ2])]});var subQ4=sQuery(id+"F0.wireOp",EDGE,"E39.bottom");Q5=makeQuery(id+"F10.boolean.opBoolean","SPLIT",EDGE,{"disambiguationData":[TD([makeQuery(id+"F1.opExtrude","CAP_FACE",FACE,{"disambiguationData":[OSD([sQuery(id+"F0.wireOp",EDGE,"E0.bottom"),sQuery(id+"F0.wireOp",EDGE,"E0.left"),sQuery(id+"F0.wireOp",EDGE,"E0.right"),sQuery(id+"F0.wireOp",EDGE,"E6"),sQuery(id+"F0.wireOp",EDGE,"E12.MirrorC"),sQuery(id+"F0.wireOp",EDGE,"E13"),sQuery(id+"F0.wireOp",EDGE,"E14"),sQuery(id+"F0.wireOp",EDGE,"E15"),sQuery(id+"F0.wireOp",EDGE,"E16"),sQuery(id+"F0.wireOp",EDGE,"E17.MirrorCS"),sQuery(id+"F0.wireOp",EDGE,"E18.MirrorCS"),sQuery(id+"F0.wireOp",EDGE,"E19.MirrorCS"),sQuery(id+"F0.wireOp",EDGE,"E21"),subQ0,subQ1,sQuery(id+"F0.wireOp",EDGE,"E25"),sQuery(id+"F0.wireOp",EDGE,"E26"),sQuery(id+"F0.wireOp",EDGE,"E27"),sQuery(id+"F0.wireOp",EDGE,"E29.MirrorCS"),sQuery(id+"F0.wireOp",EDGE,"E30.MirrorCS"),sQuery(id+"F0.wireOp",EDGE,"E31.MirrorCS"),sQuery(id+"F0.wireOp",EDGE,"E32.MirrorCS"),sQuery(id+"F0.wireOp",EDGE,"E33.MirrorCS"),sQuery(id+"F0.wireOp",EDGE,"E34.MirrorCS"),sQuery(id+"F0.wireOp",EDGE,"E35.MirrorCS"),sQuery(id+"F0.wireOp",EDGE,"E36.MirrorCS"),sQuery(id+"F0.wireOp",EDGE,"E37.MirrorCS"),subQ4])],"isStart":true}),makeQuery(id+"F1.opExtrude","SWEPT_FACE",FACE,{"disambiguationData":[OSD([subQ0])]}),makeQuery(id+"F1.opExtrude","SWEPT_FACE",FACE,{"disambiguationData":[OSD([subQ1])]}),makeQuery(id+"F2.opExtrude","CAP_FACE",FACE,{"disambiguationData":[OSD([sQuery(id+"F0.wireOp",EDGE,"E1"),sQuery(id+"F0.wireOp",EDGE,"E2"),subQ2,sQuery(id+"F0.wireOp",EDGE,"E5"),subQ4])],"isStart":true}),makeQuery(id+"F2.opExtrude","CAP_FACE",FACE,{"disambiguationData":[OSD([sQuery(id+"F0.wireOp",EDGE,"E8.MirrorCS"),sQuery(id+"F0.wireOp",EDGE,"E9.MirrorCS"),sQuery(id+"F0.wireOp",EDGE,"E10.MirrorCS"),sQuery(id+"F0.wireOp",EDGE,"E11.MirrorC"),subQ4])],"isStart":true}),subQ3,makeQuery(id+"F6.opPattern","COPY",FACE,{"derivedFrom":subQ3,"instanceName":"1"}),makeQuery(id+"F10.opExtrude","SWEPT_FACE",FACE,{"disambiguationData":[OSD([sQuery(id+"F7.wireOp",EDGE,"E64")])]})])],"derivedFrom":makeQuery(id+"F1.opExtrude","SWEPT_EDGE",EDGE,{"disambiguationData":[OSD([subQ0,subQ1])]})});}
            var Q6;
            {var subQ0=sQuery(id+"F0.wireOp",EDGE,"E22");var subQ1=sQuery(id+"F0.wireOp",EDGE,"E23");Q6=makeQuery(id+"F10.boolean.opBoolean","SPLIT",EDGE,{"disambiguationData":[TD([makeQuery(id+"F1.opExtrude","CAP_FACE",FACE,{"disambiguationData":[OSD([sQuery(id+"F0.wireOp",EDGE,"E0.bottom"),sQuery(id+"F0.wireOp",EDGE,"E0.left"),sQuery(id+"F0.wireOp",EDGE,"E0.right"),sQuery(id+"F0.wireOp",EDGE,"E6"),sQuery(id+"F0.wireOp",EDGE,"E12.MirrorC"),sQuery(id+"F0.wireOp",EDGE,"E13"),sQuery(id+"F0.wireOp",EDGE,"E14"),sQuery(id+"F0.wireOp",EDGE,"E15"),sQuery(id+"F0.wireOp",EDGE,"E16"),sQuery(id+"F0.wireOp",EDGE,"E17.MirrorCS"),sQuery(id+"F0.wireOp",EDGE,"E18.MirrorCS"),sQuery(id+"F0.wireOp",EDGE,"E19.MirrorCS"),sQuery(id+"F0.wireOp",EDGE,"E21"),subQ0,subQ1,sQuery(id+"F0.wireOp",EDGE,"E25"),sQuery(id+"F0.wireOp",EDGE,"E26"),sQuery(id+"F0.wireOp",EDGE,"E27"),sQuery(id+"F0.wireOp",EDGE,"E29.MirrorCS"),sQuery(id+"F0.wireOp",EDGE,"E30.MirrorCS"),sQuery(id+"F0.wireOp",EDGE,"E31.MirrorCS"),sQuery(id+"F0.wireOp",EDGE,"E32.MirrorCS"),sQuery(id+"F0.wireOp",EDGE,"E33.MirrorCS"),sQuery(id+"F0.wireOp",EDGE,"E34.MirrorCS"),sQuery(id+"F0.wireOp",EDGE,"E35.MirrorCS"),sQuery(id+"F0.wireOp",EDGE,"E36.MirrorCS"),sQuery(id+"F0.wireOp",EDGE,"E37.MirrorCS"),sQuery(id+"F0.wireOp",EDGE,"E39.bottom")])],"isStart":false}),makeQuery(id+"F1.opExtrude","SWEPT_FACE",FACE,{"disambiguationData":[OSD([subQ0])]}),makeQuery(id+"F1.opExtrude","SWEPT_FACE",FACE,{"disambiguationData":[OSD([subQ1])]}),makeQuery(id+"F10.opExtrude","SWEPT_FACE",FACE,{"disambiguationData":[OSD([sQuery(id+"F7.wireOp",EDGE,"E65")])]})])],"derivedFrom":makeQuery(id+"F1.opExtrude","SWEPT_EDGE",EDGE,{"disambiguationData":[OSD([subQ0,subQ1])]})});}
            var Q7;
            Q7=makeQuery(id+"F1.opExtrude","SWEPT_EDGE",EDGE,{"disambiguationData":[OSD([sQuery(id+"F0.wireOp",EDGE,"E0.bottom"),sQuery(id+"F0.wireOp",EDGE,"E21")])]});
            var Q8;
            Q8=makeQuery(id+"F1.opExtrude","SWEPT_EDGE",EDGE,{"disambiguationData":[OSD([sQuery(id+"F0.wireOp",EDGE,"E17.MirrorCS"),sQuery(id+"F0.wireOp",EDGE,"E18.MirrorCS")])]});
            var Q9;
            {var subQ0=sQuery(id+"F0.wireOp",EDGE,"E21");var subQ1=sQuery(id+"F0.wireOp",EDGE,"E22");Q9=makeQuery(id+"F10.boolean.opBoolean","SPLIT",EDGE,{"disambiguationData":[TD([makeQuery(id+"F1.opExtrude","SWEPT_FACE",FACE,{"disambiguationData":[OSD([subQ0])]}),makeQuery(id+"F1.opExtrude","SWEPT_FACE",FACE,{"disambiguationData":[OSD([subQ1])]}),makeQuery(id+"F10.opExtrude","SWEPT_FACE",FACE,{"disambiguationData":[OSD([sQuery(id+"F7.wireOp",EDGE,"E64")])]}),makeQuery(id+"F10.opExtrude","SWEPT_FACE",FACE,{"disambiguationData":[OSD([sQuery(id+"F7.wireOp",EDGE,"E65")])]})])],"derivedFrom":makeQuery(id+"F1.opExtrude","SWEPT_EDGE",EDGE,{"disambiguationData":[OSD([subQ0,subQ1])]})});}
            var Q10;
            {var subQ0=sQuery(id+"F0.wireOp",EDGE,"E22");var subQ1=sQuery(id+"F0.wireOp",EDGE,"E23");Q10=makeQuery(id+"F10.boolean.opBoolean","SPLIT",EDGE,{"disambiguationData":[TD([makeQuery(id+"F1.opExtrude","SWEPT_FACE",FACE,{"disambiguationData":[OSD([subQ0])]}),makeQuery(id+"F1.opExtrude","SWEPT_FACE",FACE,{"disambiguationData":[OSD([subQ1])]}),makeQuery(id+"F10.opExtrude","SWEPT_FACE",FACE,{"disambiguationData":[OSD([sQuery(id+"F7.wireOp",EDGE,"E64")])]}),makeQuery(id+"F10.opExtrude","SWEPT_FACE",FACE,{"disambiguationData":[OSD([sQuery(id+"F7.wireOp",EDGE,"E65")])]})])],"derivedFrom":makeQuery(id+"F1.opExtrude","SWEPT_EDGE",EDGE,{"disambiguationData":[OSD([subQ0,subQ1])]})});}
            var Q11;
            Q11=makeQuery(id+"F1.opExtrude","SWEPT_EDGE",EDGE,{"disambiguationData":[OSD([sQuery(id+"F0.wireOp",EDGE,"E0.bottom"),sQuery(id+"F0.wireOp",EDGE,"E23")])]});
            fillet(context, id + "F12", {"entities" : qUnion([Q0, Q1, Q2, Q3, Q4, Q5, Q6, Q7, Q8, Q9, Q10, Q11]), "radius" : 5 * mm, "allowEdgeOverflow" : false});
        }
        {
            var Q0;
            Q0=makeQuery(id+"F1.opExtrude","SWEPT_EDGE",EDGE,{"disambiguationData":[OSD([sQuery(id+"F0.wireOp",EDGE,"E0.bottom"),sQuery(id+"F0.wireOp",EDGE,"E18.MirrorCS")])]});
            var Q1;
            Q1=makeQuery(id+"F1.opExtrude","SWEPT_EDGE",EDGE,{"disambiguationData":[OSD([sQuery(id+"F0.wireOp",EDGE,"E0.bottom"),sQuery(id+"F0.wireOp",EDGE,"E16")])]});
            var Q2;
            Q2=makeQuery(id+"F1.opExtrude","SWEPT_EDGE",EDGE,{"disambiguationData":[OSD([sQuery(id+"F0.wireOp",EDGE,"E15"),sQuery(id+"F0.wireOp",EDGE,"E29.MirrorCS")])]});
            var Q3;
            Q3=makeQuery(id+"F1.opExtrude","SWEPT_EDGE",EDGE,{"disambiguationData":[OSD([sQuery(id+"F0.wireOp",EDGE,"E17.MirrorCS"),sQuery(id+"F0.wireOp",EDGE,"E35.MirrorCS")])]});
            fillet(context, id + "F13", {"entities" : qUnion([Q0, Q1, Q2, Q3]), "radius" : 2 * mm, "tangentPropagation" : true, "allowEdgeOverflow" : false});
        }
        {
            var Q0;
            Q0=makeQuery(id+"F5.opExtrude","CAP_FACE",FACE,{"disambiguationData":[OSD([sQuery(id+"F0.wireOp",EDGE,"E2"),sQuery(id+"F0.wireOp",EDGE,"E3"),sQuery(id+"F4.wireOp",EDGE,"E57.0"),sQuery(id+"F4.wireOp",EDGE,"E58"),sQuery(id+"F4.wireOp",EDGE,"E59")])],"isStart":false});
            var sketch = newSketch(context, id + "F14", { "sketchPlane" : qUnion([Q0])});
            skLineSegment(sketch, "E68", {"start": v(5, 0) * mm, "end": v(255.57, 0) * mm});
            skLineSegment(sketch, "E69", {"start": v(5, -25) * mm, "end": v(15.2, -25) * mm});
            skLineSegment(sketch, "E70", {"start": v(15.2, -25) * mm, "end": v(255.57, -5.98) * mm});
            skArc(sketch, "E71", {"start": v(255.57, -5.98) * mm, "mid": v(258.33, -3) * mm, "end": v(255.57, 0) * mm});
            skSolve(sketch);
        }
        {
            var Q0;
            Q0=makeQuery(id+"F14.imprint","IMPRINT",FACE,{"disambiguationData":[TD([[makeQuery(id+"F14.imprint","IMPRINT",EDGE,{"derivedFrom":sQuery(id+"F14.wireOp",EDGE,"E69")}),1.0]])]});
            var Q1;
            Q1=makeQuery(id+"F14.imprint","IMPRINT",FACE,{"disambiguationData":[TD([[makeQuery(id+"F14.imprint","IMPRINT",EDGE,{"derivedFrom":makeQuery(id+"F5.opExtrude","CAP_EDGE",EDGE,{"disambiguationData":[OSD([sQuery(id+"F4.wireOp",EDGE,"E58")])],"isStart":false})}),1.0]])]});
            extrude(context, id + "F15", {"entities" : qUnion([Q0, Q1]), "depth" : 5 * mm});
        }
        {
            var Q0;
            Q0=makeQuery(id+"F15.opExtrude","SWEPT_BODY",BODY,{"disambiguationData":[OSD([sQuery(id+"F4.wireOp",EDGE,"E57.0"),sQuery(id+"F4.wireOp",EDGE,"E59"),sQuery(id+"F14.wireOp",EDGE,"E68"),sQuery(id+"F14.wireOp",EDGE,"E69"),sQuery(id+"F14.wireOp",EDGE,"E70"),sQuery(id+"F14.wireOp",EDGE,"E71")])]});
            var Q1;
            Q1=qCreatedBy(makeId("Right.planeOp"),FACE);
            mirror(context, id + "F16", {"entities" : qUnion([Q0]), "mirrorPlane" : qUnion([Q1])});
        }
        {
            var Q0;
            {var subQ7=sQuery(id+"F0.wireOp",EDGE,"E1");Q0=makeQuery(id+"F0.imprint","IMPRINT",FACE,{"disambiguationData":[TD([[makeQuery(id+"F0.imprint","IMPRINT",EDGE,{"derivedFrom":subQ7}),1.0]])]});}
            var Q1;
            {var subQ2=sQuery(id+"F0.wireOp",EDGE,"E1");Q1=makeQuery(id+"F0.imprint","IMPRINT",FACE,{"disambiguationData":[TD([[makeQuery(id+"F0.imprint","IMPRINT",EDGE,{"derivedFrom":subQ2}),-1.0]])]});}
            var Q2;
            {var subQ2=sQuery(id+"F0.wireOp",EDGE,"E8.MirrorCS");Q2=makeQuery(id+"F0.imprint","IMPRINT",FACE,{"disambiguationData":[TD([[makeQuery(id+"F0.imprint","IMPRINT",EDGE,{"derivedFrom":subQ2}),1.0]])]});}
            extrude(context, id + "F17", {"entities" : qUnion([Q0, Q1, Q2]), "depth" : 6 * mm});
        }
    });
